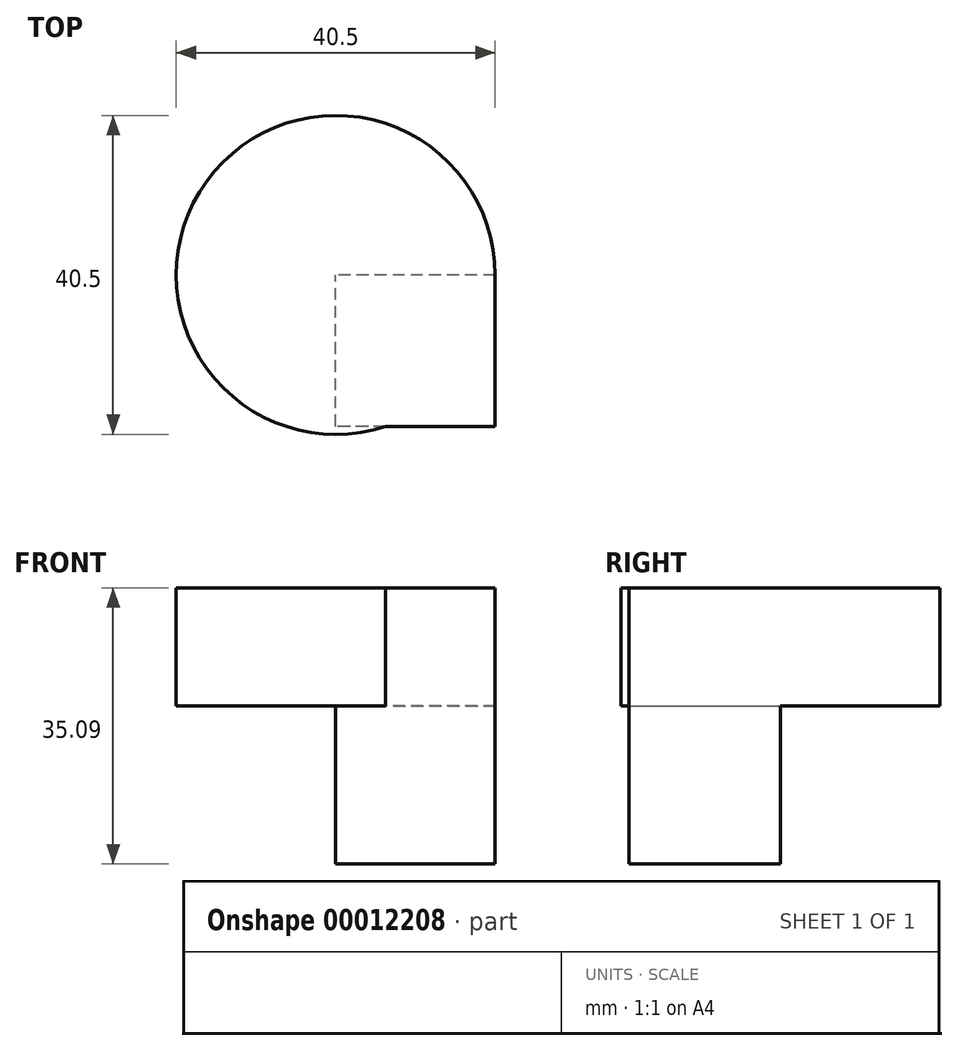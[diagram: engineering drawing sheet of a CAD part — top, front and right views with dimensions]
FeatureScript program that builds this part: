
annotation { "Feature Type Name" : "Feature", "Feature Type Description" : "" }
export const myFeature = defineFeature(function(context is Context, id is Id, definition is map)
    precondition{}
    {
        {
            var Q0;
            Q0=qCreatedBy(makeId("Front.planeOp"),FACE);
            var sketch = newSketch(context, id + "F0", { "sketchPlane" : qUnion([Q0])});
            skLineSegment(sketch, "E0.bottom", {"start": v(0, 0) * mm, "end": v(20.25, 0) * mm});
            skLineSegment(sketch, "E0.top", {"start": v(0, 14.98) * mm, "end": v(20.25, 14.98) * mm});
            skLineSegment(sketch, "E0.left", {"start": v(0, 0) * mm, "end": v(0, 14.98) * mm});
            skLineSegment(sketch, "E0.right", {"start": v(20.25, 0) * mm, "end": v(20.25, 14.98) * mm});
            skLineSegment(sketch, "E1.bottom", {"start": v(20.25, 0) * mm, "end": v(0, 0) * mm});
            skLineSegment(sketch, "E1.top", {"start": v(20.25, -20.1) * mm, "end": v(0, -20.1) * mm});
            skLineSegment(sketch, "E1.left", {"start": v(20.25, 0) * mm, "end": v(20.25, -20.1) * mm});
            skLineSegment(sketch, "E1.right", {"start": v(0, 0) * mm, "end": v(0, -20.1) * mm});
            skSolve(sketch);
        }
        {
            var Q0;
            Q0=makeQuery(id+"F0.imprint","IMPRINT",FACE,{"disambiguationData":[TD([[makeQuery(id+"F0.imprint","IMPRINT",EDGE,{"derivedFrom":sQuery(id+"F0.wireOp",EDGE,"E0.top")}),-1.0]])]});
            var Q1;
            Q1=sQuery(id+"F0.wireOp",EDGE,"E0.left");
            revolve(context, id + "F1", {"entities" : qUnion([Q0]), "axis" : qUnion([Q1]), "revolveType" : RevolveType.FULL});
        }
        {
            var Q0;
            Q0 = qSketchRegion(id + "F0", true);
            extrude(context, id + "F2", {"entities" : qUnion([Q0]), "operationType" : NewBodyOperationType.ADD, "depth" : 19.24 * mm});
        }
    });
